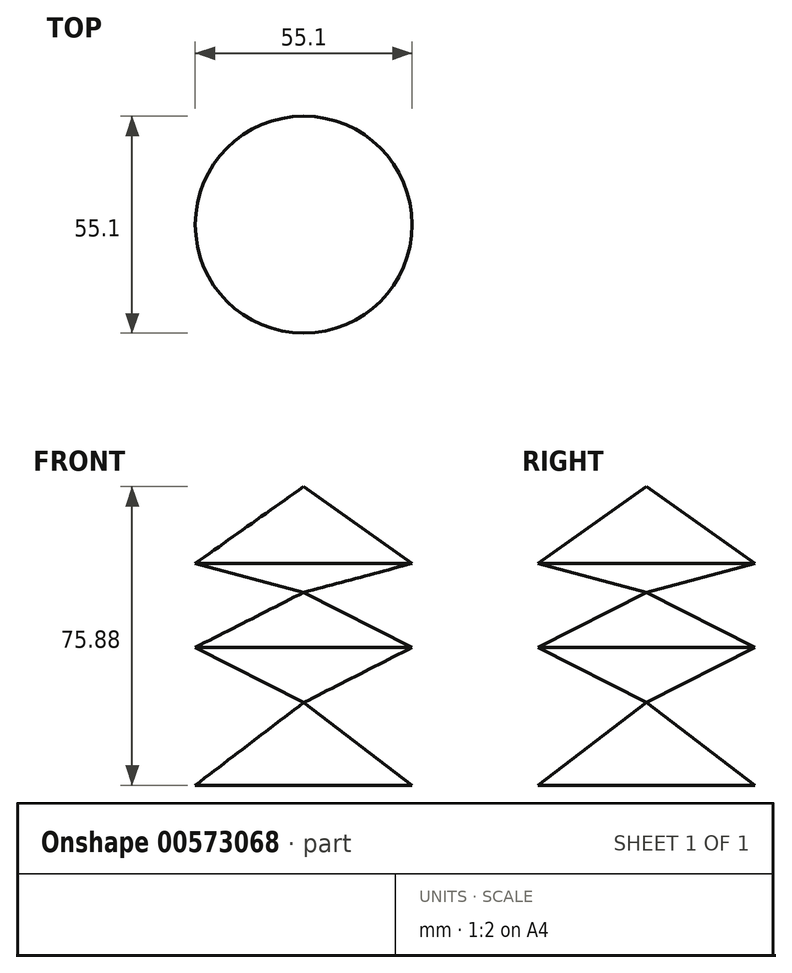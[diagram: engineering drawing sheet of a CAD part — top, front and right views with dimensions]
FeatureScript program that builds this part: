
annotation { "Feature Type Name" : "Feature", "Feature Type Description" : "" }
export const myFeature = defineFeature(function(context is Context, id is Id, definition is map)
    precondition{}
    {
        {
            var Q0;
            Q0=qCreatedBy(makeId("Front.planeOp"),FACE);
            var sketch = newSketch(context, id + "F0", { "sketchPlane" : qUnion([Q0])});
            skLineSegment(sketch, "E0", {"start": v(0, 0) * mm, "end": v(-27.55, 0) * mm});
            skLineSegment(sketch, "E1", {"start": v(-27.55, 0) * mm, "end": v(0, 21) * mm});
            skLineSegment(sketch, "E2", {"start": v(0, 21) * mm, "end": v(-27.55, 35.01) * mm});
            skLineSegment(sketch, "E3", {"start": v(-27.55, 35.01) * mm, "end": v(0, 49.02) * mm});
            skLineSegment(sketch, "E4", {"start": v(0, 49.02) * mm, "end": v(-27.55, 56.36) * mm});
            skLineSegment(sketch, "E5", {"start": v(-27.55, 56.36) * mm, "end": v(0, 75.88) * mm});
            skLineSegment(sketch, "E6", {"start": v(0, 75.88) * mm, "end": v(0, 0) * mm});
            skSolve(sketch);
        }
        {
            var Q0;
            {var subQ0=sQuery(id+"F0.wireOp",EDGE,"E2");Q0=makeQuery(id+"F0.imprint","IMPRINT",FACE,{"disambiguationData":[TD([[makeQuery(id+"F0.imprint","IMPRINT",EDGE,{"derivedFrom":subQ0}),-1.0]])]});}
            var Q1;
            {var subQ0=sQuery(id+"F0.wireOp",EDGE,"E0");Q1=makeQuery(id+"F0.imprint","IMPRINT",FACE,{"disambiguationData":[TD([[makeQuery(id+"F0.imprint","IMPRINT",EDGE,{"derivedFrom":subQ0}),-1.0]])]});}
            var Q2;
            {var subQ0=sQuery(id+"F0.wireOp",EDGE,"E4");Q2=makeQuery(id+"F0.imprint","IMPRINT",FACE,{"disambiguationData":[TD([[makeQuery(id+"F0.imprint","IMPRINT",EDGE,{"derivedFrom":subQ0}),-1.0]])]});}
            var Q3;
            Q3=sQuery(id+"F0.wireOp",EDGE,"E6");
            revolve(context, id + "F1", {"entities" : qUnion([Q0, Q1, Q2]), "axis" : qUnion([Q3]), "revolveType" : RevolveType.FULL});
        }
    });
